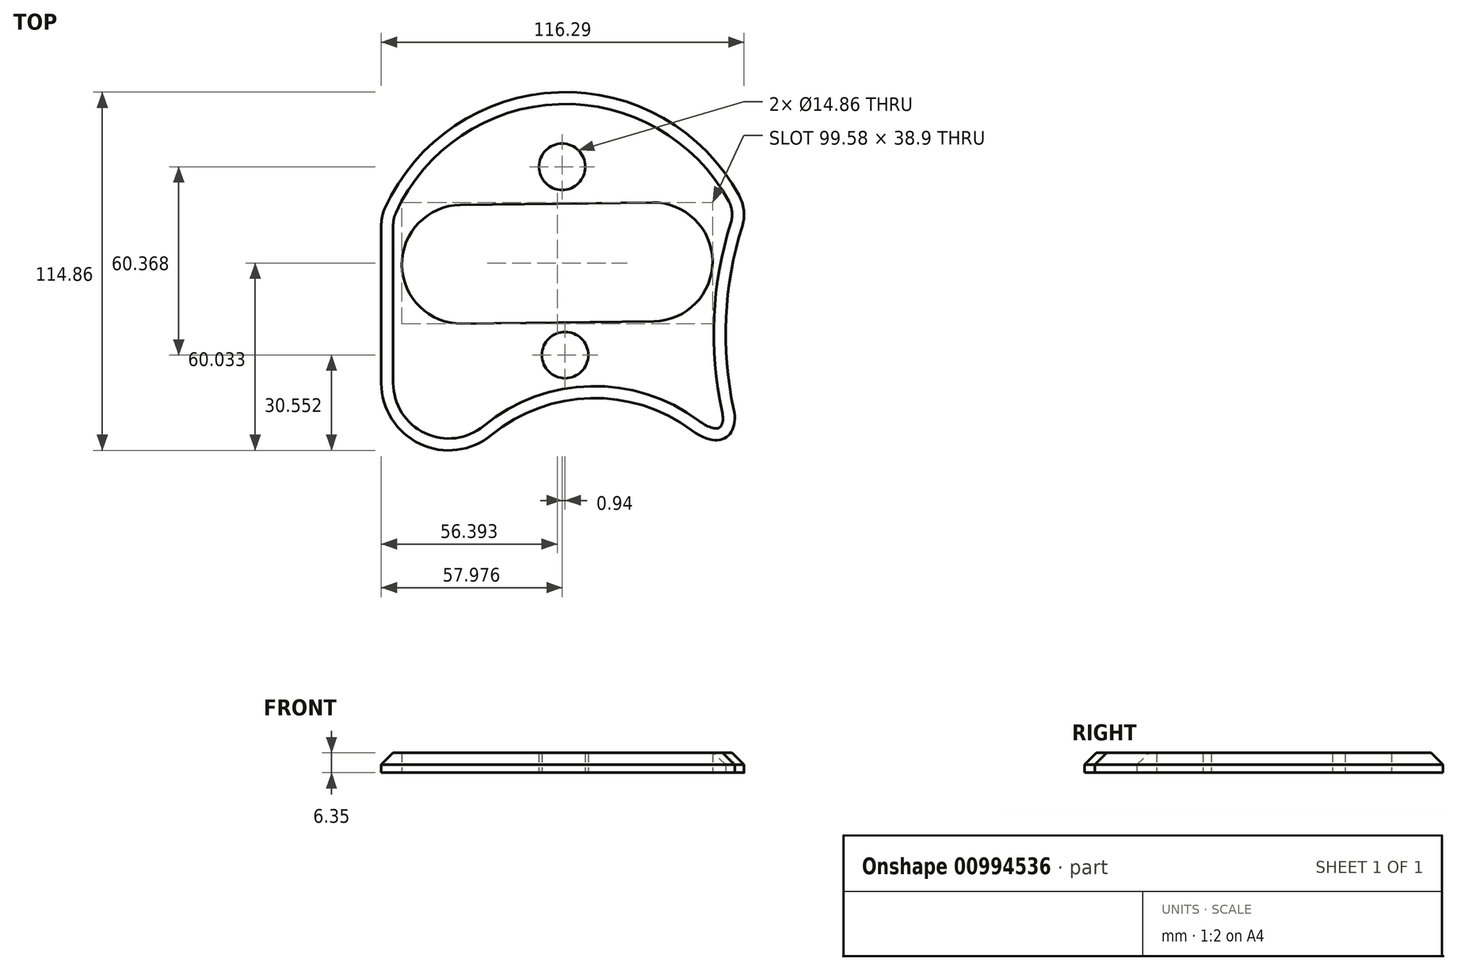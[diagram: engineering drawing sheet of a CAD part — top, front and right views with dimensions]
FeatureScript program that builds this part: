
annotation { "Feature Type Name" : "Feature", "Feature Type Description" : "" }
export const myFeature = defineFeature(function(context is Context, id is Id, definition is map)
    precondition{}
    {
        {
            var Q0;
            Q0=qCreatedBy(makeId("Top.planeOp"),FACE);
            var sketch = newSketch(context, id + "F0", { "sketchPlane" : qUnion([Q0])});
            skLineSegment(sketch, "E0", {"start": v(83.73, -16.16) * mm, "end": v(-94.14, -22.14) * mm, "construction": true});
            skSolve(sketch);
        }
        {
            var Q0;
            Q0=qCreatedBy(makeId("Top.planeOp"),FACE);
            var sketch = newSketch(context, id + "F1", { "sketchPlane" : qUnion([Q0])});
            skLineSegment(sketch, "E1", {"start": v(-58.23, 57.67) * mm, "end": v(-58.23, 4.33) * mm});
            skArc(sketch, "E2", {"start": v(59.06, 59.2) * mm, "mid": v(-0.1, 97.6) * mm, "end": v(-58.23, 57.67) * mm});
            skArc(sketch, "E3", {"start": v(59.06, 59.2) * mm, "mid": v(56.15, -9.75) * mm, "end": v(93.45, -67.8) * mm});
            skArc(sketch, "E4", {"start": v(-58.23, 4.33) * mm, "mid": v(-45.86, -15.2) * mm, "end": v(-22.93, -12.35) * mm});
            skArc(sketch, "E5", {"start": v(58.35, -32.86) * mm, "mid": v(22.9, -2.07) * mm, "end": v(-22.93, -12.35) * mm});
            skFitSpline(sketch, "E6", {"points": [v(54.77, -4.09) * mm, v(41.32, -10.85) * mm], "startDerivative": vector(5.5, -25.39) * mm, "endDerivative": vector(-27.4, 20.47) * mm});
            skSolve(sketch);
        }
        {
            var Q0;
            Q0=qCreatedBy(makeId("Top.planeOp"),FACE);
            var sketch = newSketch(context, id + "F2", { "sketchPlane" : qUnion([Q0])});
            skCircle(sketch, "E7", {"center": v(-0.25, 73.66) * mm, "radius": 7.43 * mm});
            skCircle(sketch, "E8", {"center": v(0.69, 13.3) * mm, "radius": 7.43 * mm});
            skArc(sketch, "E9", {"start": v(-32.83, 61.42) * mm, "mid": v(-51.63, 42.12) * mm, "end": v(-32.33, 23.32) * mm});
            skArc(sketch, "E10", {"start": v(29.15, 24.13) * mm, "mid": v(47.95, 43.42) * mm, "end": v(28.66, 62.22) * mm});
            skLineSegment(sketch, "E11", {"start": v(-32.83, 61.42) * mm, "end": v(28.66, 62.22) * mm});
            skLineSegment(sketch, "E12", {"start": v(-32.33, 23.32) * mm, "end": v(29.15, 24.13) * mm});
            skSolve(sketch);
        }
        {
            var Q0;
            Q0=makeQuery(id+"F1.imprint","IMPRINT",FACE,{"disambiguationData":[TD([[makeQuery(id+"F1.imprint","IMPRINT",EDGE,{"derivedFrom":sQuery(id+"F1.wireOp",EDGE,"E1")}),1.0]])]});
            extrude(context, id + "F3", {"entities" : qUnion([Q0]), "depth" : 6.35 * mm, "offsetDistance" : 25.4 * mm});
        }
        {
            var Q0;
            Q0=makeQuery(id+"F2.imprint","IMPRINT",FACE,{"disambiguationData":[TD([[makeQuery(id+"F2.imprint","IMPRINT",EDGE,{"derivedFrom":sQuery(id+"F2.wireOp",EDGE,"E7")}),1.0]])]});
            var Q1;
            Q1=makeQuery(id+"F2.imprint","IMPRINT",FACE,{"disambiguationData":[TD([[makeQuery(id+"F2.imprint","IMPRINT",EDGE,{"derivedFrom":sQuery(id+"F2.wireOp",EDGE,"E9")}),1.0]])]});
            var Q2;
            Q2=makeQuery(id+"F2.imprint","IMPRINT",FACE,{"disambiguationData":[TD([[makeQuery(id+"F2.imprint","IMPRINT",EDGE,{"derivedFrom":sQuery(id+"F2.wireOp",EDGE,"E8")}),1.0]])]});
            extrude(context, id + "F4", {"entities" : qUnion([Q0, Q1, Q2]), "operationType" : NewBodyOperationType.REMOVE, "depth" : 25.4 * mm, "offsetDistance" : 25.4 * mm});
        }
        {
            var Q0;
            Q0=makeQuery(id+"F3.opExtrude","SWEPT_EDGE",EDGE,{"disambiguationData":[OSD([sQuery(id+"F1.wireOp",EDGE,"E1"),sQuery(id+"F1.wireOp",EDGE,"E2")])]});
            var Q1;
            Q1=makeQuery(id+"F3.opExtrude","SWEPT_EDGE",EDGE,{"disambiguationData":[OSD([sQuery(id+"F1.wireOp",EDGE,"E2"),sQuery(id+"F1.wireOp",EDGE,"E3")])]});
            fillet(context, id + "F5", {"entities" : qUnion([Q0, Q1]), "radius" : 12.7 * mm, "tangentPropagation" : true, "allowEdgeOverflow" : false});
        }
        {
            var Q0;
            Q0=makeQuery(id+"F3.opExtrude","CAP_EDGE",EDGE,{"disambiguationData":[OSD([sQuery(id+"F1.wireOp",EDGE,"E2")])],"isStart":false});
            chamfer(context, id + "F6", {"entities" : qUnion([Q0]), "width" : 3.8 * mm, "tangentPropagation" : true});
        }
    });
